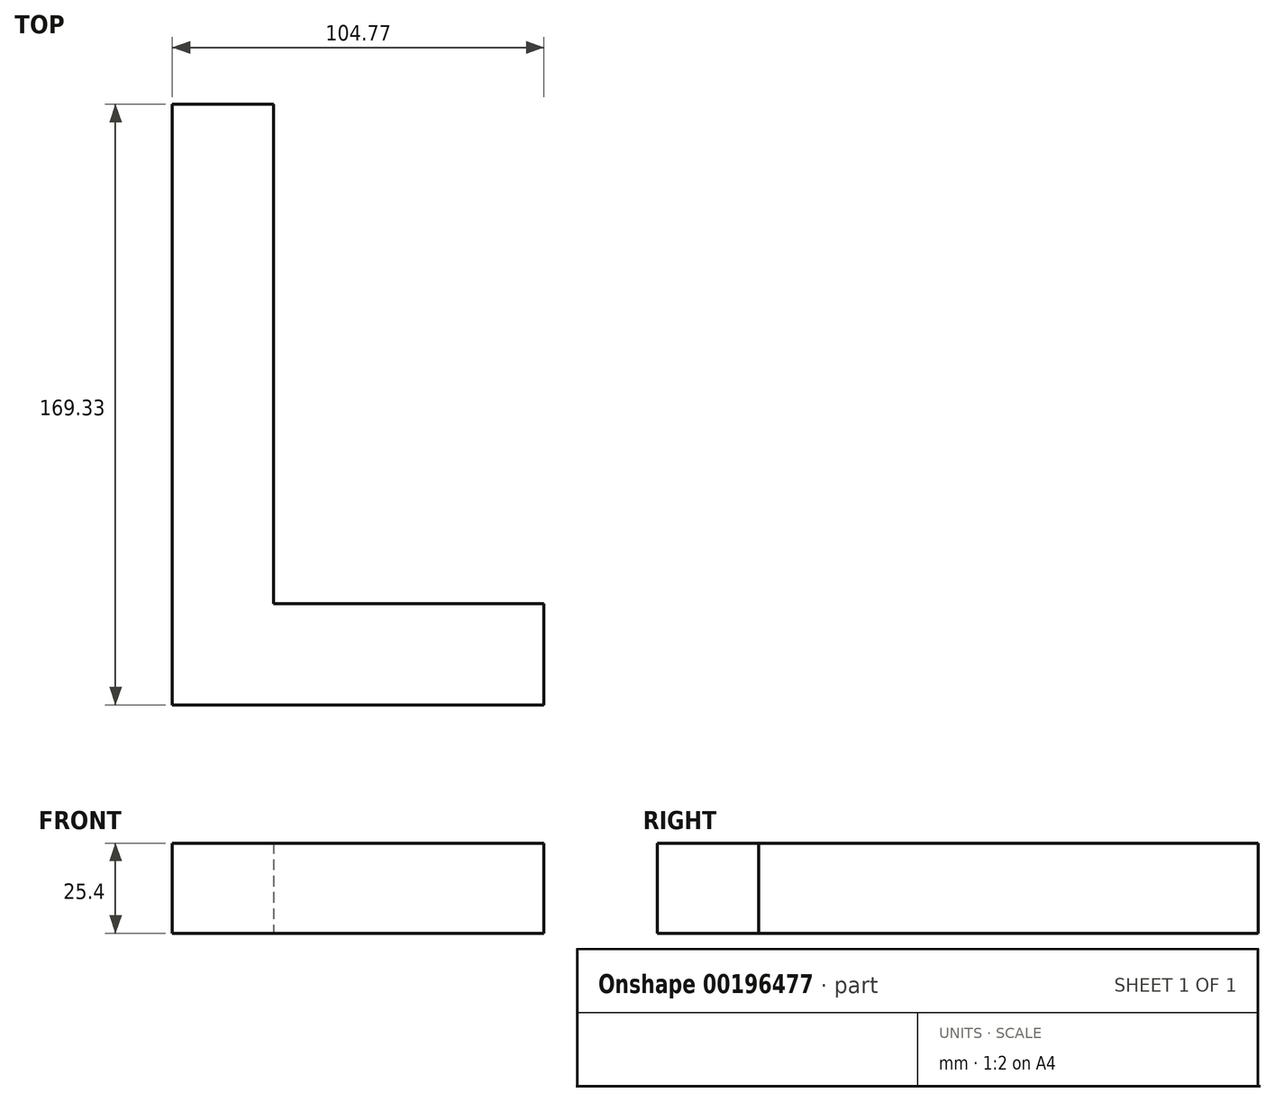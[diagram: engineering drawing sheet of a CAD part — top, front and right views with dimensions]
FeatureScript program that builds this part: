
annotation { "Feature Type Name" : "Feature", "Feature Type Description" : "" }
export const myFeature = defineFeature(function(context is Context, id is Id, definition is map)
    precondition{}
    {
        {
            var Q0;
            Q0=qCreatedBy(makeId("Top.planeOp"),FACE);
            var sketch = newSketch(context, id + "F0", { "sketchPlane" : qUnion([Q0])});
            skLineSegment(sketch, "E0", {"start": v(0, 0) * mm, "end": v(0, 169.33) * mm});
            skLineSegment(sketch, "E1", {"start": v(0, 169.33) * mm, "end": v(28.58, 169.33) * mm});
            skLineSegment(sketch, "E2", {"start": v(28.58, 169.33) * mm, "end": v(28.58, 28.58) * mm});
            skLineSegment(sketch, "E3", {"start": v(28.58, 28.58) * mm, "end": v(104.78, 28.58) * mm});
            skLineSegment(sketch, "E4", {"start": v(104.78, 28.57) * mm, "end": v(104.78, 0) * mm});
            skLineSegment(sketch, "E5", {"start": v(104.78, 0) * mm, "end": v(0, 0) * mm});
            skSolve(sketch);
        }
        {
            var Q0;
            Q0 = qSketchRegion(id + "F0", true);
            extrude(context, id + "F1", {"entities" : qUnion([Q0]), "depth" : 25.4 * mm});
        }
    });
